# Revit family: Shower-Steam_Generator-KOHLER-Invigoration_Series-K-32326_1
name_source: partatom
category: Plumbing Fixtures
units: mm (PartAtom-declared; Revit-internal decimal feet)

## family parameters
Cut with Voids When Loaded = No
Host = Face
OmniClass Number = 23.21.29.19.19
OmniClass Title = Steam Room Equipment
Part Type = Normal
Room Calculation Point = No
Round Connector Dimension = Use Diameter
Shared = No

## types (1)
- NA-Stainless
    ADA Compliant = No
    Apparent Load = 9000 VA
    Assembly Code = D2010
    CW Connection = Yes
    Cold Water Inlet = Cold Water Inlet
    Date Modified = 04/29/2024
    Default Elevation = 0"
    Description = 9 KW Steam Generator
    Drain Included = Yes
    Electrical Connector = Yes
    Electrical Note = One Dedicated Circuit Required
    Finish = Kohler-Metal-NA-Stainless
    Flow Rate = 0 GPM
    HW Connection = Yes
    Handle Clearance 1 = 2 9/16"
    Handle Clearance 2 = 1 3/8"
    Height = 13"
    Hot Water Inlet = Hot Water Inlet
    Length = 6 3/8"
    Manufacturer = Kohler Co.
    Master Format 2014 = 22 41 39
    Master Format 2014 Name = Residential Faucets, Supplies, and Trim
    Material = Premium Metal Construction
    Model = K-32326-NA
    Pressure = 0.00 psi
    Pressure Relief = Pressure Relief
    Product Documentation Link = https://www.us.kohler.com
    Product Name = Invigoration Series
    Product Page URL = http://www.us.kohler.com
    Steam Connection = Yes
    Steam Outlet = Steam Outlet
    Type = 1
    URL = https://www.us.kohler.com
    Vent Connection = Yes
    Voltage = 0 V
    Waste Connection = Yes
    Waste Water Outlet = Waste Water Outlet
    WaterSense Certified = No
    Width = 19 15/16"

## geometry (parser evidence)
native form markers: Sweep x5
no freeform markers — native parametric forms only
